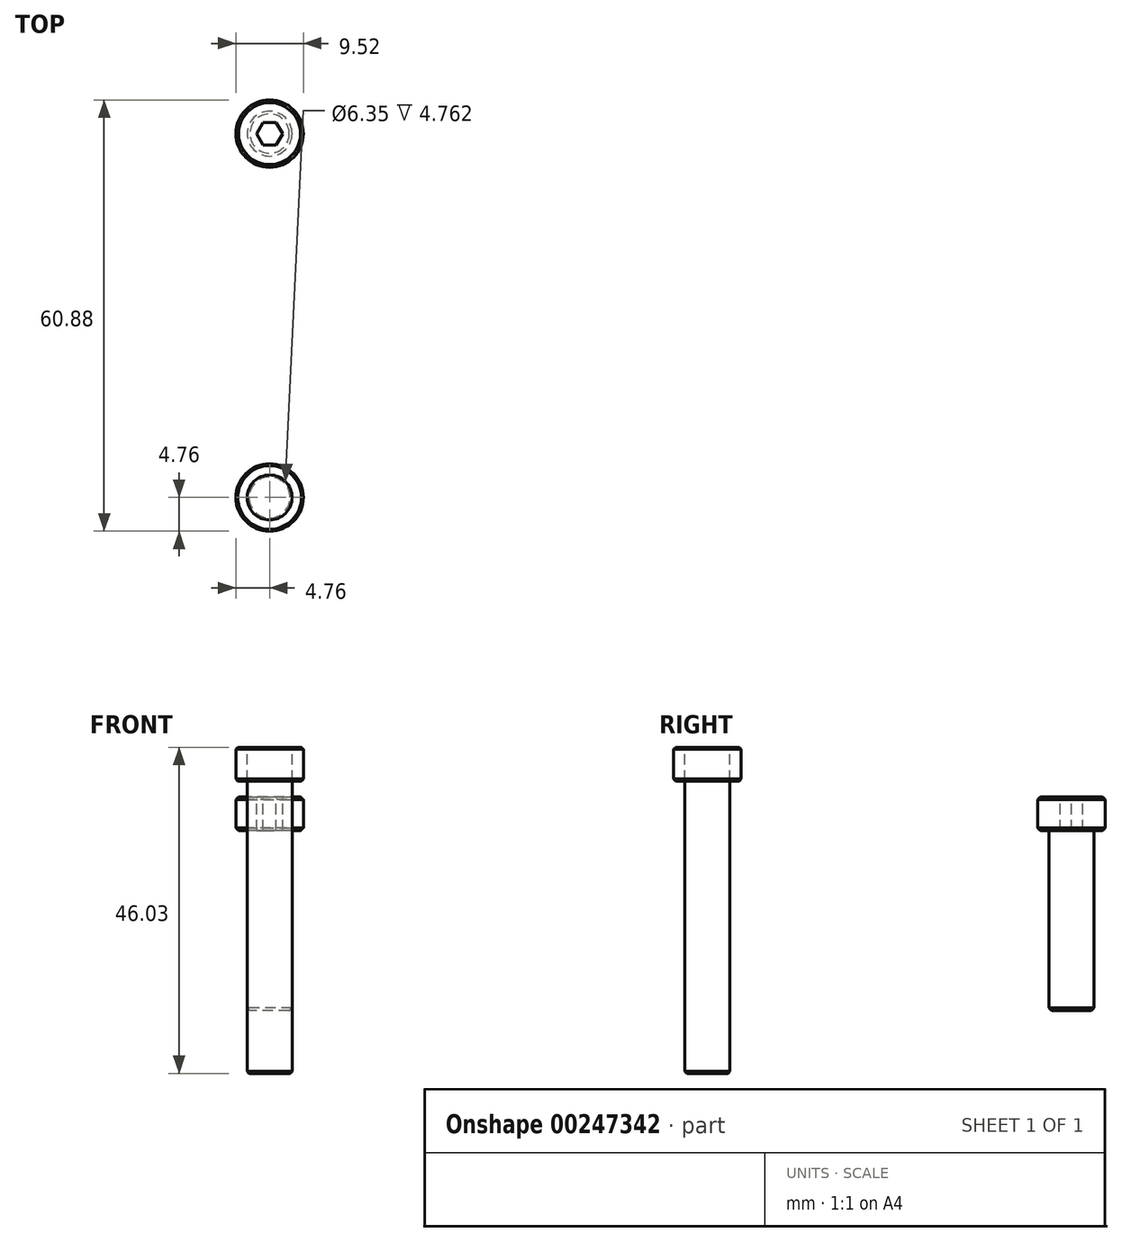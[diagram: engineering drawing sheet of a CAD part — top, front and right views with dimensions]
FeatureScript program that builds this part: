
annotation { "Feature Type Name" : "Feature", "Feature Type Description" : "" }
export const myFeature = defineFeature(function(context is Context, id is Id, definition is map)
    precondition{}
    {
        {
            var Q0;
            Q0=qCreatedBy(makeId("Front.planeOp"),FACE);
            var sketch = newSketch(context, id + "F0", { "sketchPlane" : qUnion([Q0])});
            skLineSegment(sketch, "E0.bottom", {"start": v(0, 10.94) * mm, "end": v(3.18, 10.94) * mm});
            skLineSegment(sketch, "E0.top", {"start": v(0, -35.1) * mm, "end": v(2.9, -35.1) * mm});
            skLineSegment(sketch, "E0.left", {"start": v(0, 10.94) * mm, "end": v(0, -35.1) * mm});
            skLineSegment(sketch, "E0.right", {"start": v(3.18, 10.94) * mm, "end": v(3.18, -34.81) * mm});
            skLineSegment(sketch, "E1.bottom", {"start": v(0, 10.94) * mm, "end": v(4.48, 10.94) * mm});
            skLineSegment(sketch, "E1.top", {"start": v(0, 6.18) * mm, "end": v(4.48, 6.18) * mm});
            skLineSegment(sketch, "E1.left", {"start": v(0, 10.94) * mm, "end": v(0, 6.18) * mm});
            skLineSegment(sketch, "E1.right", {"start": v(4.76, 10.66) * mm, "end": v(4.76, 6.46) * mm});
            skLineSegment(sketch, "E2.MirrorCS", {"start": v(0, 10.94) * mm, "end": v(-3.18, 10.94) * mm});
            skLineSegment(sketch, "E3.MirrorCS", {"start": v(-4.76, 10.94) * mm, "end": v(-4.76, 6.18) * mm});
            skLineSegment(sketch, "E4.MirrorCS", {"start": v(0, -35.1) * mm, "end": v(-3.17, -35.1) * mm});
            skLineSegment(sketch, "E5.MirrorCS", {"start": v(-3.18, 10.94) * mm, "end": v(-3.17, -35.1) * mm});
            skLineSegment(sketch, "E6.MirrorCS", {"start": v(0, 10.94) * mm, "end": v(-4.76, 10.94) * mm});
            skLineSegment(sketch, "E7.MirrorCS", {"start": v(0, 6.18) * mm, "end": v(-4.76, 6.18) * mm});
            skLineSegment(sketch, "E8", {"start": v(4.48, 10.94) * mm, "end": v(4.76, 10.66) * mm});
            skLineSegment(sketch, "E9", {"start": v(4.48, 6.18) * mm, "end": v(4.76, 6.46) * mm});
            skLineSegment(sketch, "E10", {"start": v(2.9, -35.1) * mm, "end": v(3.18, -34.81) * mm});
            skPoint(sketch, "E11.orphan", {"position": v(3.18, -35.1) * mm});
            skPoint(sketch, "E12.orphan", {"position": v(4.76, 10.94) * mm});
            skPoint(sketch, "E13.orphan", {"position": v(4.76, 6.18) * mm});
            skSolve(sketch);
        }
        {
            var Q0;
            {var subQ5=sQuery(id+"F0.wireOp",EDGE,"E1.left");Q0=makeQuery(id+"F0.imprint","IMPRINT",FACE,{"disambiguationData":[TD([[makeQuery(id+"F0.imprint","IMPRINT",EDGE,{"derivedFrom":subQ5}),1.0]])]});}
            var Q1;
            {var subQ5=sQuery(id+"F0.wireOp",EDGE,"E1.right");Q1=makeQuery(id+"F0.imprint","IMPRINT",FACE,{"disambiguationData":[TD([[makeQuery(id+"F0.imprint","IMPRINT",EDGE,{"derivedFrom":subQ5}),-1.0]])]});}
            var Q2;
            {var subQ0=sQuery(id+"F0.wireOp",EDGE,"E0.top");Q2=makeQuery(id+"F0.imprint","IMPRINT",FACE,{"disambiguationData":[TD([[makeQuery(id+"F0.imprint","IMPRINT",EDGE,{"derivedFrom":subQ0}),1.0]])]});}
            var Q3;
            Q3=sQuery(id+"F0.wireOp",EDGE,"E0.left");
            revolve(context, id + "F1", {"entities" : qUnion([Q0, Q1, Q2]), "axis" : qUnion([Q3]), "revolveType" : RevolveType.FULL});
        }
        {
            var Q0;
            Q0=makeQuery(id+"F1.opRevolve","SWEPT_FACE",FACE,{"disambiguationData":[OSD([sQuery(id+"F0.wireOp",EDGE,"E1.bottom")])]});
            var sketch = newSketch(context, id + "F2", { "sketchPlane" : qUnion([Q0])});
            skCircle(sketch, "E14.cCircle", {"center": v(0, 0) * mm, "radius": 1.83 * mm, "construction": true});
            skLineSegment(sketch, "E14.0", {"start": v(0, 1.83) * mm, "end": v(1.59, 0.92) * mm});
            skLineSegment(sketch, "E14.1", {"start": v(1.59, 0.92) * mm, "end": v(1.59, -0.92) * mm});
            skLineSegment(sketch, "E14.2", {"start": v(1.59, -0.92) * mm, "end": v(0, -1.83) * mm});
            skLineSegment(sketch, "E14.3", {"start": v(0, -1.83) * mm, "end": v(-1.59, -0.92) * mm});
            skLineSegment(sketch, "E14.4", {"start": v(-1.59, -0.92) * mm, "end": v(-1.59, 0.92) * mm});
            skLineSegment(sketch, "E14.5", {"start": v(-1.59, 0.92) * mm, "end": v(0, 1.83) * mm});
            skSolve(sketch);
        }
        {
            var Q0;
            Q0 = qSketchRegion(id + "F2", true);
            extrude(context, id + "F3", {"entities" : qUnion([Q0]), "operationType" : NewBodyOperationType.REMOVE, "oppositeDirection" : true, "depth" : 3.17 * mm});
        }
        {
            var Q0;
            Q0=qCreatedBy(makeId("Right.planeOp"),FACE);
            var sketch = newSketch(context, id + "F4", { "sketchPlane" : qUnion([Q0])});
            skLineSegment(sketch, "E15.bottom", {"start": v(51.36, 3.95) * mm, "end": v(56.12, 3.95) * mm});
            skLineSegment(sketch, "E15.top", {"start": v(51.36, -0.83) * mm, "end": v(56.12, -0.83) * mm});
            skLineSegment(sketch, "E15.left", {"start": v(51.36, 3.95) * mm, "end": v(51.36, -0.83) * mm});
            skLineSegment(sketch, "E15.right", {"start": v(56.12, 3.95) * mm, "end": v(56.12, -0.83) * mm});
            skLineSegment(sketch, "E16.bottom", {"start": v(51.36, 3.95) * mm, "end": v(54.53, 3.95) * mm});
            skLineSegment(sketch, "E16.top", {"start": v(51.36, -26.23) * mm, "end": v(54.53, -26.23) * mm});
            skLineSegment(sketch, "E16.left", {"start": v(51.36, 3.95) * mm, "end": v(51.36, -26.23) * mm});
            skLineSegment(sketch, "E16.right", {"start": v(54.53, 3.95) * mm, "end": v(54.53, -26.23) * mm});
            skLineSegment(sketch, "E17.MirrorCS", {"start": v(46.6, 3.95) * mm, "end": v(46.6, -0.83) * mm});
            skLineSegment(sketch, "E18.MirrorCS", {"start": v(51.36, 3.95) * mm, "end": v(46.6, 3.95) * mm});
            skLineSegment(sketch, "E19.MirrorCS", {"start": v(51.36, -0.83) * mm, "end": v(46.6, -0.83) * mm});
            skLineSegment(sketch, "E20.MirrorCS", {"start": v(51.36, 3.95) * mm, "end": v(48.18, 3.95) * mm});
            skLineSegment(sketch, "E21.MirrorCS", {"start": v(48.18, 3.95) * mm, "end": v(48.18, -26.23) * mm});
            skLineSegment(sketch, "E22.MirrorCS", {"start": v(51.36, -26.23) * mm, "end": v(48.18, -26.23) * mm});
            skSolve(sketch);
        }
        {
            var Q0;
            {var subQ4=sQuery(id+"F4.wireOp",EDGE,"E16.bottom");Q0=makeQuery(id+"F4.imprint","IMPRINT",FACE,{"disambiguationData":[TD([[makeQuery(id+"F4.imprint","IMPRINT",EDGE,{"derivedFrom":subQ4}),-1.0]])]});}
            var Q1;
            {var subQ0=sQuery(id+"F4.wireOp",EDGE,"E15.bottom");Q1=makeQuery(id+"F4.imprint","IMPRINT",FACE,{"disambiguationData":[TD([[makeQuery(id+"F4.imprint","IMPRINT",EDGE,{"derivedFrom":subQ0}),-1.0]])]});}
            var Q2;
            {var subQ4=sQuery(id+"F4.wireOp",EDGE,"E16.top");Q2=makeQuery(id+"F4.imprint","IMPRINT",FACE,{"disambiguationData":[TD([[makeQuery(id+"F4.imprint","IMPRINT",EDGE,{"derivedFrom":subQ4}),1.0]])]});}
            var Q3;
            Q3=sQuery(id+"F4.wireOp",EDGE,"E16.left");
            revolve(context, id + "F5", {"entities" : qUnion([Q0, Q1, Q2]), "axis" : qUnion([Q3]), "revolveType" : RevolveType.FULL});
        }
        {
            var Q0;
            Q0=makeQuery(id+"F5.opRevolve","SWEPT_EDGE",EDGE,{"disambiguationData":[OSD([sQuery(id+"F4.wireOp",EDGE,"E15.bottom"),sQuery(id+"F4.wireOp",EDGE,"E15.right")])]});
            var Q1;
            Q1=makeQuery(id+"F5.opRevolve","SWEPT_EDGE",EDGE,{"disambiguationData":[OSD([sQuery(id+"F4.wireOp",EDGE,"E15.top"),sQuery(id+"F4.wireOp",EDGE,"E15.right")])]});
            var Q2;
            Q2=makeQuery(id+"F5.opRevolve","SWEPT_EDGE",EDGE,{"disambiguationData":[OSD([sQuery(id+"F4.wireOp",EDGE,"E16.top"),sQuery(id+"F4.wireOp",EDGE,"E16.right")])]});
            chamfer(context, id + "F6", {"entities" : qUnion([Q0, Q1, Q2]), "width" : 0.4 * mm, "tangentPropagation" : true});
        }
        {
            var Q0;
            Q0=makeQuery(id+"F5.opRevolve","SWEPT_FACE",FACE,{"disambiguationData":[OSD([sQuery(id+"F4.wireOp",EDGE,"E15.bottom"),sQuery(id+"F4.wireOp",EDGE,"E16.bottom")])]});
            var sketch = newSketch(context, id + "F7", { "sketchPlane" : qUnion([Q0])});
            skCircle(sketch, "E23.cCircle", {"center": v(0, 51.36) * mm, "radius": 1.59 * mm, "construction": true});
            skLineSegment(sketch, "E23.0", {"start": v(-0.92, 52.95) * mm, "end": v(0.92, 52.95) * mm});
            skLineSegment(sketch, "E23.1", {"start": v(0.92, 52.95) * mm, "end": v(1.83, 51.36) * mm});
            skLineSegment(sketch, "E23.2", {"start": v(1.83, 51.36) * mm, "end": v(0.92, 49.77) * mm});
            skLineSegment(sketch, "E23.3", {"start": v(0.92, 49.77) * mm, "end": v(-0.92, 49.77) * mm});
            skLineSegment(sketch, "E23.4", {"start": v(-0.92, 49.77) * mm, "end": v(-1.83, 51.36) * mm});
            skLineSegment(sketch, "E23.5", {"start": v(-1.83, 51.36) * mm, "end": v(-0.92, 52.95) * mm});
            skPoint(sketch, "E23.0.midPoint", {"position": v(0, 52.95) * mm});
            skSolve(sketch);
        }
        {
            var Q0;
            Q0 = qSketchRegion(id + "F7", true);
            extrude(context, id + "F8", {"entities" : qUnion([Q0]), "operationType" : NewBodyOperationType.REMOVE, "oppositeDirection" : true, "depth" : 4.78 * mm});
        }
    });
